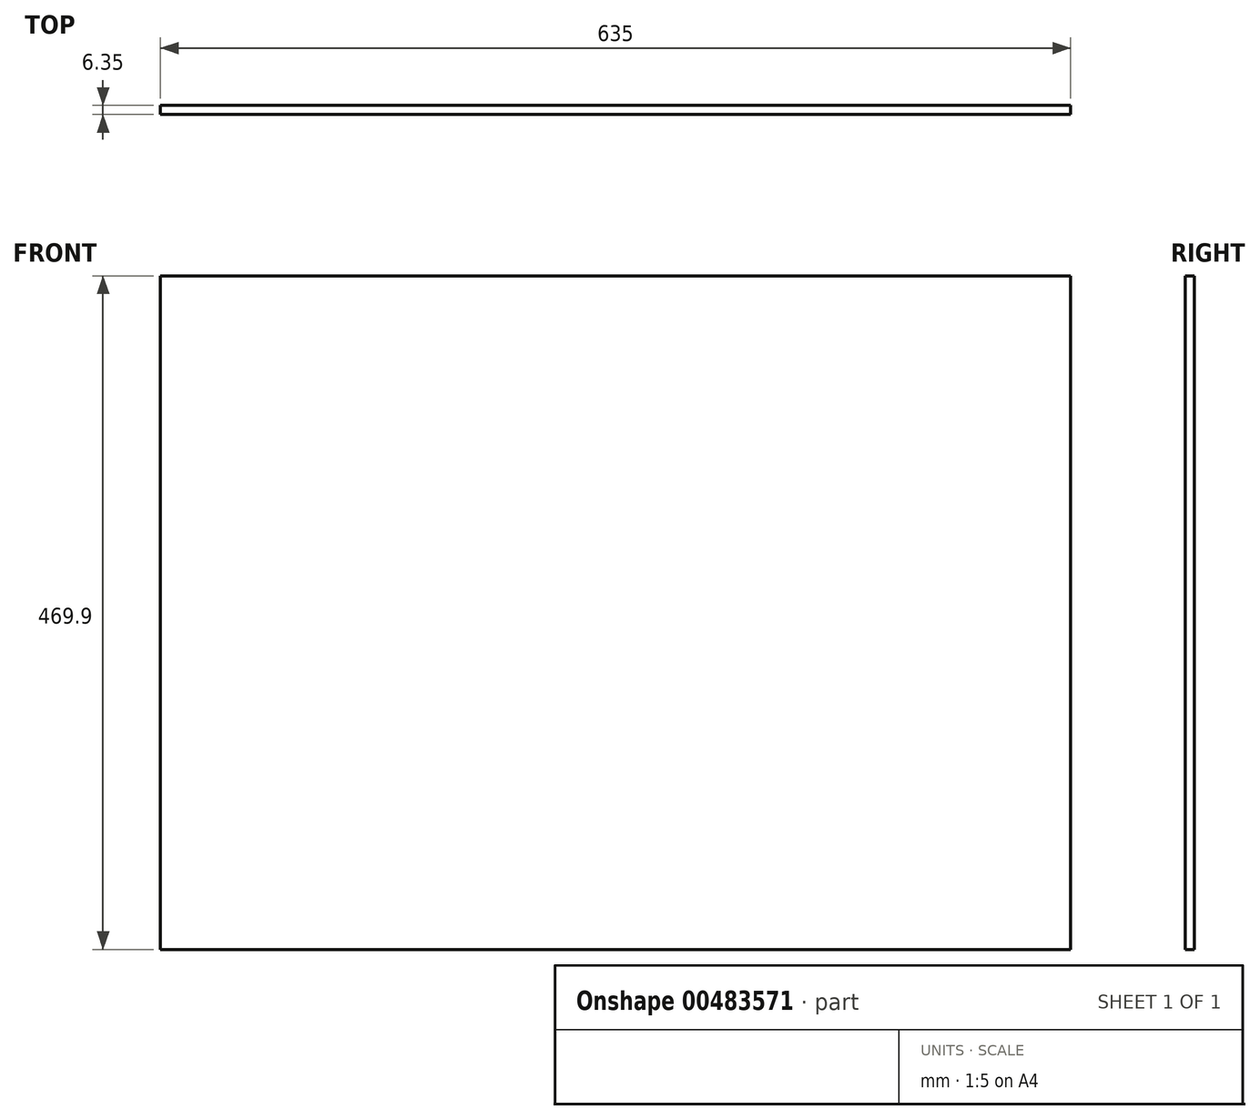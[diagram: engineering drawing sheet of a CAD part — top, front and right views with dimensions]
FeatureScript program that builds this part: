
annotation { "Feature Type Name" : "Feature", "Feature Type Description" : "" }
export const myFeature = defineFeature(function(context is Context, id is Id, definition is map)
    precondition{}
    {
        {
            var Q0;
            Q0=qCreatedBy(makeId("Front.planeOp"),FACE);
            var sketch = newSketch(context, id + "F0", { "sketchPlane" : qUnion([Q0])});
            skLineSegment(sketch, "E0.bottom", {"start": v(-459.88, -203.76) * mm, "end": v(175.12, -203.76) * mm});
            skLineSegment(sketch, "E0.top", {"start": v(-459.88, 266.14) * mm, "end": v(175.12, 266.14) * mm});
            skLineSegment(sketch, "E0.left", {"start": v(-459.88, -203.76) * mm, "end": v(-459.88, 266.14) * mm});
            skLineSegment(sketch, "E0.right", {"start": v(175.12, -203.76) * mm, "end": v(175.12, 266.14) * mm});
            skPoint(sketch, "E1.endSnap0", {"position": v(175.12, 31.2) * mm});
            skSolve(sketch);
        }
        {
            var Q0;
            Q0=makeQuery(id+"F0.imprint","IMPRINT",FACE,{"disambiguationData":[TD([[makeQuery(id+"F0.imprint","IMPRINT",EDGE,{"derivedFrom":sQuery(id+"F0.wireOp",EDGE,"E0.bottom")}),1.0]])]});
            extrude(context, id + "F1", {"entities" : qUnion([Q0]), "depth" : 6.35 * mm});
        }
    });
